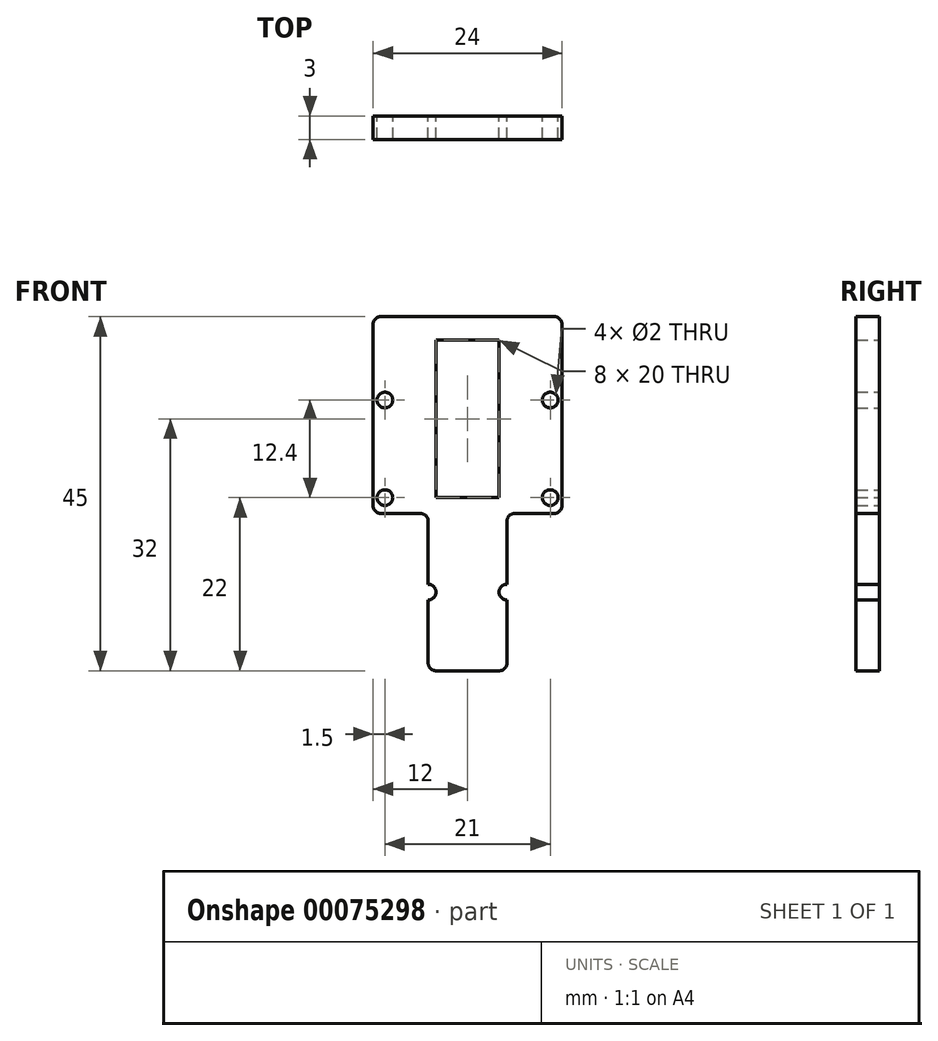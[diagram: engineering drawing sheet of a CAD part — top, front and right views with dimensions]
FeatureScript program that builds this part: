
annotation { "Feature Type Name" : "Feature", "Feature Type Description" : "" }
export const myFeature = defineFeature(function(context is Context, id is Id, definition is map)
    precondition{}
    {
        {
            var Q0;
            Q0=qCreatedBy(makeId("Front.planeOp"),FACE);
            var sketch = newSketch(context, id + "F0", { "sketchPlane" : qUnion([Q0])});
            skLineSegment(sketch, "E0.bottom", {"start": v(1, 0) * mm, "end": v(23, 0) * mm});
            skLineSegment(sketch, "E0.left", {"start": v(0, -1) * mm, "end": v(0, -24) * mm});
            skLineSegment(sketch, "E0.right", {"start": v(24, -1) * mm, "end": v(24, -24) * mm});
            skLineSegment(sketch, "E1", {"start": v(8, -45) * mm, "end": v(16, -45) * mm});
            skLineSegment(sketch, "E2", {"start": v(1, -25) * mm, "end": v(6, -25) * mm});
            skLineSegment(sketch, "E3", {"start": v(7, -26) * mm, "end": v(7, -34) * mm});
            skLineSegment(sketch, "E4", {"start": v(17, -44) * mm, "end": v(17, -36) * mm});
            skLineSegment(sketch, "E5", {"start": v(18, -25) * mm, "end": v(23, -25) * mm});
            skCircle(sketch, "E6", {"center": v(22.5, -23) * mm, "radius": 1 * mm});
            skCircle(sketch, "E7", {"center": v(1.5, -23) * mm, "radius": 1 * mm});
            skLineSegment(sketch, "E8", {"start": v(1.5, -23) * mm, "end": v(0, -23) * mm, "construction": true});
            skLineSegment(sketch, "E9", {"start": v(22.5, -23) * mm, "end": v(24, -23) * mm, "construction": true});
            skCircle(sketch, "E10", {"center": v(1.5, -10.6) * mm, "radius": 1 * mm});
            skCircle(sketch, "E11", {"center": v(22.5, -10.6) * mm, "radius": 1 * mm});
            skLineSegment(sketch, "E12", {"start": v(1.5, -10.6) * mm, "end": v(0, -10.6) * mm, "construction": true});
            skLineSegment(sketch, "E13", {"start": v(22.5, -10.6) * mm, "end": v(24, -10.6) * mm, "construction": true});
            skLineSegment(sketch, "E14.bottom", {"start": v(8, -3) * mm, "end": v(16, -3) * mm});
            skLineSegment(sketch, "E14.top", {"start": v(8, -23) * mm, "end": v(16, -23) * mm});
            skLineSegment(sketch, "E14.left", {"start": v(8, -3) * mm, "end": v(8, -23) * mm});
            skLineSegment(sketch, "E14.right", {"start": v(16, -3) * mm, "end": v(16, -23) * mm});
            skPoint(sketch, "E15", {"position": v(12, 0) * mm});
            skPoint(sketch, "E16", {"position": v(12, -3) * mm});
            skLineSegment(sketch, "E17", {"start": v(12, 0) * mm, "end": v(12, -3) * mm, "construction": true});
            skArc(sketch, "E18", {"start": v(7, -36) * mm, "mid": v(8, -35) * mm, "end": v(7, -34) * mm});
            skArc(sketch, "E19", {"start": v(17, -34) * mm, "mid": v(16, -35) * mm, "end": v(17, -36) * mm});
            skLineSegment(sketch, "E20.trimOffspring", {"start": v(7, -36) * mm, "end": v(7, -44) * mm});
            skLineSegment(sketch, "E21.trimOffspring", {"start": v(17, -34) * mm, "end": v(17, -26) * mm});
            skPoint(sketch, "E22.visualSharp", {"position": v(0, 0) * mm});
            skArc(sketch, "E22.filletArc", {"start": v(1, 0) * mm, "mid": v(0.3, -0.3) * mm, "end": v(0, -1) * mm});
            skPoint(sketch, "E23.visualSharp", {"position": v(24, 0) * mm});
            skArc(sketch, "E23.filletArc", {"start": v(24, -1) * mm, "mid": v(23.7, -0.3) * mm, "end": v(23, 0) * mm});
            skPoint(sketch, "E24.visualSharp", {"position": v(24, -25) * mm});
            skArc(sketch, "E24.filletArc", {"start": v(23, -25) * mm, "mid": v(23.7, -24.7) * mm, "end": v(24, -24) * mm});
            skPoint(sketch, "E25.visualSharp", {"position": v(0, -25) * mm});
            skArc(sketch, "E25.filletArc", {"start": v(0, -24) * mm, "mid": v(0.3, -24.7) * mm, "end": v(1, -25) * mm});
            skPoint(sketch, "E26.visualSharp", {"position": v(7, -25) * mm});
            skArc(sketch, "E26.filletArc", {"start": v(7, -26) * mm, "mid": v(6.7, -25.3) * mm, "end": v(6, -25) * mm});
            skPoint(sketch, "E27.visualSharp", {"position": v(17, -25) * mm});
            skArc(sketch, "E27.filletArc", {"start": v(18, -25) * mm, "mid": v(17.3, -25.3) * mm, "end": v(17, -26) * mm});
            skPoint(sketch, "E28.visualSharp", {"position": v(17, -45) * mm});
            skArc(sketch, "E28.filletArc", {"start": v(16, -45) * mm, "mid": v(16.7, -44.7) * mm, "end": v(17, -44) * mm});
            skPoint(sketch, "E29.visualSharp", {"position": v(7, -45) * mm});
            skArc(sketch, "E29.filletArc", {"start": v(7, -44) * mm, "mid": v(7.3, -44.7) * mm, "end": v(8, -45) * mm});
            skSolve(sketch);
        }
        {
            var Q0;
            Q0 = qSketchRegion(id + "F0", true);
            extrude(context, id + "F1", {"entities" : qUnion([Q0]), "depth" : 3 * mm});
        }
    });
